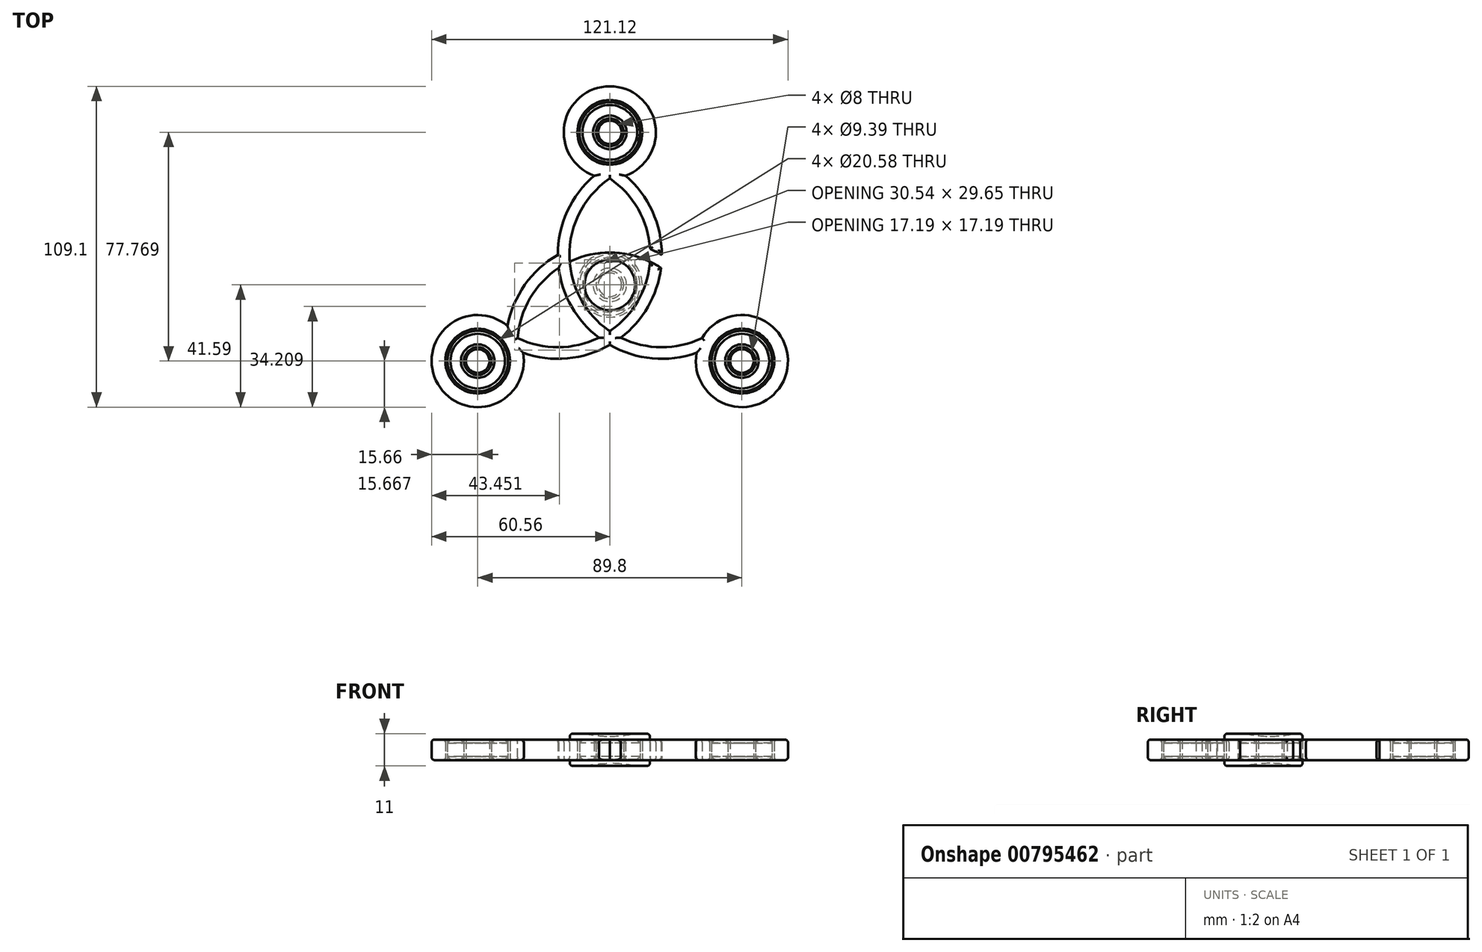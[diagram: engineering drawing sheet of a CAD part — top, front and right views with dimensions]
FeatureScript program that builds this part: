
annotation { "Feature Type Name" : "Feature", "Feature Type Description" : "" }
export const myFeature = defineFeature(function(context is Context, id is Id, definition is map)
    precondition{}
    {
        {
            var Q0;
            Q0=qCreatedBy(makeId("Front.planeOp"),FACE);
            var sketch = newSketch(context, id + "F0", { "sketchPlane" : qUnion([Q0])});
            skLineSegment(sketch, "E0", {"start": v(0, 0) * mm, "end": v(0, 16.34) * mm, "construction": true});
            skSolve(sketch);
        }
        {
            var Q0;
            Q0=qCreatedBy(makeId("Top.planeOp"),FACE);
            var sketch = newSketch(context, id + "F1", { "sketchPlane" : qUnion([Q0])});
            skCircle(sketch, "E1.cCircle", {"center": v(0, 0) * mm, "radius": 40.85 * mm, "construction": true});
            skLineSegment(sketch, "E1.0", {"start": v(0, 40.85) * mm, "end": v(35.37, -20.42) * mm, "construction": true});
            skLineSegment(sketch, "E1.1", {"start": v(35.37, -20.42) * mm, "end": v(-35.37, -20.42) * mm, "construction": true});
            skLineSegment(sketch, "E1.2", {"start": v(-35.37, -20.42) * mm, "end": v(0, 40.85) * mm, "construction": true});
            skCircle(sketch, "E2", {"center": v(0, 40.85) * mm, "radius": 11 * mm, "construction": true});
            skCircle(sketch, "E3", {"center": v(35.37, -20.42) * mm, "radius": 11 * mm, "construction": true});
            skCircle(sketch, "E4", {"center": v(-35.37, -20.42) * mm, "radius": 11 * mm, "construction": true});
            skCircle(sketch, "E5", {"center": v(0, 0) * mm, "radius": 11 * mm, "construction": true});
            skArc(sketch, "E6", {"start": v(10.27, 44.8) * mm, "mid": v(-15.33, -2.5) * mm, "end": v(35.37, -20.42) * mm});
            skArc(sketch, "E7", {"start": v(-35.37, -20.42) * mm, "mid": v(15.33, -2.5) * mm, "end": v(-10.27, 44.8) * mm});
            skArc(sketch, "E8", {"start": v(35.37, -20.42) * mm, "mid": v(0, 14.95) * mm, "end": v(-35.37, -20.42) * mm});
            skLineSegment(sketch, "E9", {"start": v(-35.37, -20.42) * mm, "end": v(-12.95, -7.48) * mm, "construction": true});
            skLineSegment(sketch, "E10.trimOffspring", {"start": v(-9.53, -5.5) * mm, "end": v(0, 0) * mm, "construction": true});
            skLineSegment(sketch, "E11", {"start": v(-12.95, -7.48) * mm, "end": v(-9.53, -5.5) * mm, "construction": true});
            skArc(sketch, "E12.0", {"start": v(11.1, 40.94) * mm, "mid": v(-11.27, -2) * mm, "end": v(35.1, -15.95) * mm});
            skArc(sketch, "E13.0", {"start": v(30.75, -26.88) * mm, "mid": v(-1.6, 10.96) * mm, "end": v(-29.93, -29.98) * mm});
            skArc(sketch, "E14.0", {"start": v(-41, -10.86) * mm, "mid": v(-40.97, -10.9) * mm, "end": v(-40.93, -10.93) * mm});
            skArc(sketch, "E15.trimOffspring", {"start": v(40.93, -10.93) * mm, "mid": v(40.97, -10.9) * mm, "end": v(41, -10.86) * mm});
            skArc(sketch, "E16.trimOffspring", {"start": v(-35.1, -15.95) * mm, "mid": v(11.27, -2) * mm, "end": v(-11.1, 40.94) * mm});
            skLineSegment(sketch, "E17", {"start": v(0, 40.85) * mm, "end": v(0, 36.18) * mm, "construction": true});
            skSolve(sketch);
        }
        {
            var Q0;
            {var subQ0=sQuery(id+"F1.wireOp",EDGE,"E13.0");var subQ1=sQuery(id+"F1.wireOp",EDGE,"E6");var subQ2=makeQuery(id+"F1.imprint","INTERSECT",VERTEX,{"disambiguationData":[OD(0.0)],"derivedFrom":[subQ1,subQ0]});Q0=makeQuery(id+"F1.imprint","IMPRINT",FACE,{"disambiguationData":[TD([[makeQuery(id+"F1.imprint","IMPRINT",EDGE,{"disambiguationData":[TD([[subQ2,1.0]])],"derivedFrom":subQ1}),1.0]])]});}
            var Q1;
            {var subQ0=sQuery(id+"F1.wireOp",EDGE,"E7");var subQ1=sQuery(id+"F1.wireOp",EDGE,"E6");var subQ2=makeQuery(id+"F1.imprint","INTERSECT",VERTEX,{"disambiguationData":[OD(1.0)],"derivedFrom":[subQ1,subQ0]});Q1=makeQuery(id+"F1.imprint","IMPRINT",FACE,{"disambiguationData":[TD([[makeQuery(id+"F1.imprint","IMPRINT",EDGE,{"disambiguationData":[TD([[subQ2,1.0]])],"derivedFrom":subQ1}),1.0]])]});}
            var Q2;
            {var subQ0=sQuery(id+"F1.wireOp",EDGE,"E7");var subQ1=sQuery(id+"F1.wireOp",EDGE,"E6");var subQ2=makeQuery(id+"F1.imprint","INTERSECT",VERTEX,{"disambiguationData":[OD(1.0)],"derivedFrom":[subQ1,subQ0]});Q2=makeQuery(id+"F1.imprint","IMPRINT",FACE,{"disambiguationData":[TD([[makeQuery(id+"F1.imprint","IMPRINT",EDGE,{"disambiguationData":[TD([[subQ2,1.0]])],"derivedFrom":subQ1}),-1.0]])]});}
            var Q3;
            {var subQ0=sQuery(id+"F1.wireOp",EDGE,"E8");var subQ1=sQuery(id+"F1.wireOp",EDGE,"E7");var subQ2=makeQuery(id+"F1.imprint","INTERSECT",VERTEX,{"disambiguationData":[OD(0.0)],"derivedFrom":[subQ1,subQ0]});Q3=makeQuery(id+"F1.imprint","IMPRINT",FACE,{"disambiguationData":[TD([[makeQuery(id+"F1.imprint","IMPRINT",EDGE,{"disambiguationData":[TD([[subQ2,-1.0]])],"derivedFrom":subQ1}),1.0]])]});}
            var Q4;
            {var subQ0=sQuery(id+"F1.wireOp",EDGE,"E8");var subQ1=sQuery(id+"F1.wireOp",EDGE,"E6");var subQ2=makeQuery(id+"F1.imprint","INTERSECT",VERTEX,{"disambiguationData":[OD(1.0)],"derivedFrom":[subQ1,subQ0]});Q4=makeQuery(id+"F1.imprint","IMPRINT",FACE,{"disambiguationData":[TD([[makeQuery(id+"F1.imprint","IMPRINT",EDGE,{"disambiguationData":[TD([[subQ2,-1.0]])],"derivedFrom":subQ1}),-1.0]])]});}
            var Q5;
            {var subQ0=sQuery(id+"F1.wireOp",EDGE,"E13.0");var subQ1=sQuery(id+"F1.wireOp",EDGE,"E6");var subQ2=makeQuery(id+"F1.imprint","INTERSECT",VERTEX,{"disambiguationData":[OD(1.0)],"derivedFrom":[subQ1,subQ0]});Q5=makeQuery(id+"F1.imprint","IMPRINT",FACE,{"disambiguationData":[TD([[makeQuery(id+"F1.imprint","IMPRINT",EDGE,{"disambiguationData":[TD([[subQ2,-1.0]])],"derivedFrom":subQ1}),1.0]])]});}
            var Q6;
            {var subQ0=sQuery(id+"F1.wireOp",EDGE,"E8");var subQ1=sQuery(id+"F1.wireOp",EDGE,"E6");var subQ2=makeQuery(id+"F1.imprint","INTERSECT",VERTEX,{"disambiguationData":[OD(1.0)],"derivedFrom":[subQ1,subQ0]});Q6=makeQuery(id+"F1.imprint","IMPRINT",FACE,{"disambiguationData":[TD([[makeQuery(id+"F1.imprint","IMPRINT",EDGE,{"disambiguationData":[TD([[subQ2,-1.0]])],"derivedFrom":subQ1}),1.0]])]});}
            var Q7;
            {var subQ0=sQuery(id+"F1.wireOp",EDGE,"E12.0");var subQ1=sQuery(id+"F1.wireOp",EDGE,"E7");var subQ2=makeQuery(id+"F1.imprint","INTERSECT",VERTEX,{"disambiguationData":[OD(1.0)],"derivedFrom":[subQ1,subQ0]});Q7=makeQuery(id+"F1.imprint","IMPRINT",FACE,{"disambiguationData":[TD([[makeQuery(id+"F1.imprint","IMPRINT",EDGE,{"disambiguationData":[TD([[subQ2,-1.0]])],"derivedFrom":subQ1}),1.0]])]});}
            var Q8;
            {var subQ0=sQuery(id+"F1.wireOp",EDGE,"E8");var subQ1=sQuery(id+"F1.wireOp",EDGE,"E6");var subQ2=makeQuery(id+"F1.imprint","INTERSECT",VERTEX,{"disambiguationData":[OD(0.0)],"derivedFrom":[subQ1,subQ0]});Q8=makeQuery(id+"F1.imprint","IMPRINT",FACE,{"disambiguationData":[TD([[makeQuery(id+"F1.imprint","IMPRINT",EDGE,{"disambiguationData":[TD([[subQ2,1.0]])],"derivedFrom":subQ1}),1.0]])]});}
            var Q9;
            {var subQ0=sQuery(id+"F1.wireOp",EDGE,"E8");var subQ1=sQuery(id+"F1.wireOp",EDGE,"E7");var subQ2=makeQuery(id+"F1.imprint","INTERSECT",VERTEX,{"disambiguationData":[OD(1.0)],"derivedFrom":[subQ1,subQ0]});Q9=makeQuery(id+"F1.imprint","IMPRINT",FACE,{"disambiguationData":[TD([[makeQuery(id+"F1.imprint","IMPRINT",EDGE,{"disambiguationData":[TD([[subQ2,1.0]])],"derivedFrom":subQ1}),-1.0]])]});}
            var Q10;
            {var subQ0=sQuery(id+"F1.wireOp",EDGE,"E8");var subQ1=sQuery(id+"F1.wireOp",EDGE,"E7");var subQ2=makeQuery(id+"F1.imprint","INTERSECT",VERTEX,{"disambiguationData":[OD(1.0)],"derivedFrom":[subQ1,subQ0]});Q10=makeQuery(id+"F1.imprint","IMPRINT",FACE,{"disambiguationData":[TD([[makeQuery(id+"F1.imprint","IMPRINT",EDGE,{"disambiguationData":[TD([[subQ2,1.0]])],"derivedFrom":subQ1}),1.0]])]});}
            var Q11;
            {var subQ0=sQuery(id+"F1.wireOp",EDGE,"E16.trimOffspring");var subQ1=sQuery(id+"F1.wireOp",EDGE,"E8");var subQ2=makeQuery(id+"F1.imprint","INTERSECT",VERTEX,{"disambiguationData":[OD(1.0)],"derivedFrom":[subQ1,subQ0]});Q11=makeQuery(id+"F1.imprint","IMPRINT",FACE,{"disambiguationData":[TD([[makeQuery(id+"F1.imprint","IMPRINT",EDGE,{"disambiguationData":[TD([[subQ2,-1.0]])],"derivedFrom":subQ1}),1.0]])]});}
            var Q12;
            {var subQ0=sQuery(id+"F1.wireOp",EDGE,"E16.trimOffspring");var subQ1=sQuery(id+"F1.wireOp",EDGE,"E6");var subQ2=makeQuery(id+"F1.imprint","INTERSECT",VERTEX,{"disambiguationData":[OD(0.0)],"derivedFrom":[subQ1,subQ0]});Q12=makeQuery(id+"F1.imprint","IMPRINT",FACE,{"disambiguationData":[TD([[makeQuery(id+"F1.imprint","IMPRINT",EDGE,{"disambiguationData":[TD([[subQ2,-1.0]])],"derivedFrom":subQ1}),1.0]])]});}
            var Q13;
            {var subQ0=sQuery(id+"F1.wireOp",EDGE,"E7");var subQ1=sQuery(id+"F1.wireOp",EDGE,"E6");var subQ2=makeQuery(id+"F1.imprint","INTERSECT",VERTEX,{"disambiguationData":[OD(0.0)],"derivedFrom":[subQ1,subQ0]});Q13=makeQuery(id+"F1.imprint","IMPRINT",FACE,{"disambiguationData":[TD([[makeQuery(id+"F1.imprint","IMPRINT",EDGE,{"disambiguationData":[TD([[subQ2,-1.0]])],"derivedFrom":subQ1}),1.0]])]});}
            var Q14;
            {var subQ0=sQuery(id+"F1.wireOp",EDGE,"E12.0");var subQ1=sQuery(id+"F1.wireOp",EDGE,"E7");var subQ2=makeQuery(id+"F1.imprint","INTERSECT",VERTEX,{"disambiguationData":[OD(0.0)],"derivedFrom":[subQ1,subQ0]});Q14=makeQuery(id+"F1.imprint","IMPRINT",FACE,{"disambiguationData":[TD([[makeQuery(id+"F1.imprint","IMPRINT",EDGE,{"disambiguationData":[TD([[subQ2,1.0]])],"derivedFrom":subQ1}),1.0]])]});}
            extrude(context, id + "F2", {"entities" : qUnion([Q0, Q1, Q2, Q3, Q4, Q5, Q6, Q7, Q8, Q9, Q10, Q11, Q12, Q13, Q14]), "endBound" : BoundingType.SYMMETRIC, "depth" : 7 * mm, "offsetDistance" : 25 * mm});
        }
        {
            var Q0;
            Q0=qCreatedBy(makeId("Top.planeOp"),FACE);
            var sketch = newSketch(context, id + "F3", { "sketchPlane" : qUnion([Q0])});
            skLineSegment(sketch, "E18", {"start": v(0, 0) * mm, "end": v(0, 40.85) * mm, "construction": true});
            skLineSegment(sketch, "E19", {"start": v(0, 40.85) * mm, "end": v(0, 51.85) * mm, "construction": true});
            skCircle(sketch, "E20", {"center": v(0, 51.85) * mm, "radius": 11 * mm});
            skCircle(sketch, "E21.0", {"center": v(0, 51.85) * mm, "radius": 15.66 * mm});
            skCircle(sketch, "E22.1.0", {"center": v(-44.9, -25.92) * mm, "radius": 11 * mm});
            skCircle(sketch, "E22.1.1", {"center": v(-44.9, -25.92) * mm, "radius": 15.66 * mm});
            skCircle(sketch, "E22.2.0", {"center": v(44.9, -25.92) * mm, "radius": 11 * mm});
            skCircle(sketch, "E22.2.1", {"center": v(44.9, -25.92) * mm, "radius": 15.66 * mm});
            skPoint(sketch, "E22.center", {"position": v(0, 0) * mm});
            skSolve(sketch);
        }
        {
            var Q0;
            Q0 = qSketchRegion(id + "F3", true);
            extrude(context, id + "F4", {"entities" : qUnion([Q0]), "operationType" : NewBodyOperationType.ADD, "endBound" : BoundingType.SYMMETRIC, "depth" : 7 * mm, "offsetDistance" : 25 * mm});
        }
        {
            var Q0;
            Q0=makeQuery(id+"F4.boolean.opBoolean","MERGE",FACE,{"derivedFrom":[makeQuery(id+"F2.opExtrude","CAP_FACE",FACE,{"disambiguationData":[OSD([sQuery(id+"F1.wireOp",EDGE,"E6"),sQuery(id+"F1.wireOp",EDGE,"E7"),sQuery(id+"F1.wireOp",EDGE,"E8"),sQuery(id+"F1.wireOp",EDGE,"E12.0"),sQuery(id+"F1.wireOp",EDGE,"E13.0"),sQuery(id+"F1.wireOp",EDGE,"E16.trimOffspring")])],"isStart":true}),makeQuery(id+"F4.opExtrude","CAP_FACE",FACE,{"disambiguationData":[OSD([sQuery(id+"F3.wireOp",EDGE,"E20"),sQuery(id+"F3.wireOp",EDGE,"E21.0")])],"isStart":true}),makeQuery(id+"F4.opExtrude","CAP_FACE",FACE,{"disambiguationData":[OSD([sQuery(id+"F3.wireOp",EDGE,"E22.1.0"),sQuery(id+"F3.wireOp",EDGE,"E22.1.1")])],"isStart":true}),makeQuery(id+"F4.opExtrude","CAP_FACE",FACE,{"disambiguationData":[OSD([sQuery(id+"F3.wireOp",EDGE,"E22.2.0"),sQuery(id+"F3.wireOp",EDGE,"E22.2.1")])],"isStart":true})]});
            var Q1;
            Q1=makeQuery(id+"F4.boolean.opBoolean","MERGE",FACE,{"derivedFrom":[makeQuery(id+"F2.opExtrude","CAP_FACE",FACE,{"disambiguationData":[OSD([sQuery(id+"F1.wireOp",EDGE,"E6"),sQuery(id+"F1.wireOp",EDGE,"E7"),sQuery(id+"F1.wireOp",EDGE,"E8"),sQuery(id+"F1.wireOp",EDGE,"E12.0"),sQuery(id+"F1.wireOp",EDGE,"E13.0"),sQuery(id+"F1.wireOp",EDGE,"E16.trimOffspring")])],"isStart":false}),makeQuery(id+"F4.opExtrude","CAP_FACE",FACE,{"disambiguationData":[OSD([sQuery(id+"F3.wireOp",EDGE,"E20"),sQuery(id+"F3.wireOp",EDGE,"E21.0")])],"isStart":false}),makeQuery(id+"F4.opExtrude","CAP_FACE",FACE,{"disambiguationData":[OSD([sQuery(id+"F3.wireOp",EDGE,"E22.1.0"),sQuery(id+"F3.wireOp",EDGE,"E22.1.1")])],"isStart":false}),makeQuery(id+"F4.opExtrude","CAP_FACE",FACE,{"disambiguationData":[OSD([sQuery(id+"F3.wireOp",EDGE,"E22.2.0"),sQuery(id+"F3.wireOp",EDGE,"E22.2.1")])],"isStart":false})]});
            fillet(context, id + "F5", {"entities" : qUnion([Q0, Q1]), "radius" : 1 * mm, "tangentPropagation" : true, "allowEdgeOverflow" : false});
        }
        {
            var Q0;
            Q0=qCreatedBy(makeId("Top.planeOp"),FACE);
            var sketch = newSketch(context, id + "F6", { "sketchPlane" : qUnion([Q0])});
            skCircle(sketch, "E23", {"center": v(0, 0) * mm, "radius": 11 * mm});
            skCircle(sketch, "E24", {"center": v(0, 0) * mm, "radius": 4 * mm});
            skCircle(sketch, "E25", {"center": v(0, 0) * mm, "radius": 4.7 * mm});
            skCircle(sketch, "E26", {"center": v(0, 0) * mm, "radius": 10.3 * mm});
            skSolve(sketch);
        }
        {
            var Q0;
            Q0=makeQuery(id+"F6.imprint","IMPRINT",FACE,{"disambiguationData":[TD([[makeQuery(id+"F6.imprint","IMPRINT",EDGE,{"derivedFrom":sQuery(id+"F6.wireOp",EDGE,"E24")}),-1.0]])]});
            var Q1;
            Q1=makeQuery(id+"F6.imprint","IMPRINT",FACE,{"disambiguationData":[TD([[makeQuery(id+"F6.imprint","IMPRINT",EDGE,{"derivedFrom":sQuery(id+"F6.wireOp",EDGE,"E23")}),1.0]])]});
            extrude(context, id + "F7", {"entities" : qUnion([Q0, Q1]), "operationType" : NewBodyOperationType.ADD, "endBound" : BoundingType.SYMMETRIC, "depth" : 7 * mm, "offsetDistance" : 25 * mm});
        }
        {
            var Q0;
            Q0=makeQuery(id+"F6.imprint","IMPRINT",FACE,{"disambiguationData":[TD([[makeQuery(id+"F6.imprint","IMPRINT",EDGE,{"derivedFrom":sQuery(id+"F6.wireOp",EDGE,"E25")}),-1.0]])]});
            extrude(context, id + "F8", {"entities" : qUnion([Q0]), "endBound" : BoundingType.SYMMETRIC, "depth" : 6.5 * mm, "offsetDistance" : 25 * mm});
        }
        {
            var Q0;
            Q0=makeQuery(id+"F8.opExtrude","CAP_EDGE",EDGE,{"disambiguationData":[OSD([sQuery(id+"F6.wireOp",EDGE,"E26")])],"isStart":false});
            var Q1;
            Q1=makeQuery(id+"F8.opExtrude","CAP_EDGE",EDGE,{"disambiguationData":[OSD([sQuery(id+"F6.wireOp",EDGE,"E25")])],"isStart":false});
            chamfer(context, id + "F9", {"entities" : qUnion([Q0, Q1]), "chamferType" : ChamferType.OFFSET_ANGLE, "width" : 1 * mm, "oppositeDirection" : false, "angle" : 45 * degree, "tangentPropagation" : true});
        }
        {
            var Q0;
            Q0=makeQuery(id+"F8.opExtrude","CAP_EDGE",EDGE,{"disambiguationData":[OSD([sQuery(id+"F6.wireOp",EDGE,"E25")])],"isStart":true});
            var Q1;
            Q1=makeQuery(id+"F8.opExtrude","CAP_EDGE",EDGE,{"disambiguationData":[OSD([sQuery(id+"F6.wireOp",EDGE,"E26")])],"isStart":true});
            chamfer(context, id + "F10", {"entities" : qUnion([Q0, Q1]), "width" : 1 * mm, "tangentPropagation" : true});
        }
        {
            var Q0;
            Q0=makeQuery(id+"F7.opExtrude","CAP_EDGE",EDGE,{"disambiguationData":[OSD([sQuery(id+"F6.wireOp",EDGE,"E23")])],"isStart":false});
            var Q1;
            Q1=makeQuery(id+"F7.opExtrude","CAP_EDGE",EDGE,{"disambiguationData":[OSD([sQuery(id+"F6.wireOp",EDGE,"E26")])],"isStart":false});
            fillet(context, id + "F11", {"entities" : qUnion([Q0, Q1]), "radius" : .2 * mm, "tangentPropagation" : true, "allowEdgeOverflow" : false});
        }
        {
            var Q0;
            Q0=makeQuery(id+"F7.opExtrude","CAP_EDGE",EDGE,{"disambiguationData":[OSD([sQuery(id+"F6.wireOp",EDGE,"E24")])],"isStart":false});
            var Q1;
            Q1=makeQuery(id+"F7.opExtrude","CAP_EDGE",EDGE,{"disambiguationData":[OSD([sQuery(id+"F6.wireOp",EDGE,"E25")])],"isStart":false});
            var Q2;
            Q2=makeQuery(id+"F7.opExtrude","CAP_EDGE",EDGE,{"disambiguationData":[OSD([sQuery(id+"F6.wireOp",EDGE,"E23")])],"isStart":true});
            var Q3;
            Q3=makeQuery(id+"F7.opExtrude","CAP_EDGE",EDGE,{"disambiguationData":[OSD([sQuery(id+"F6.wireOp",EDGE,"E26")])],"isStart":true});
            var Q4;
            Q4=makeQuery(id+"F7.opExtrude","CAP_EDGE",EDGE,{"disambiguationData":[OSD([sQuery(id+"F6.wireOp",EDGE,"E25")])],"isStart":true});
            var Q5;
            Q5=makeQuery(id+"F7.opExtrude","CAP_EDGE",EDGE,{"disambiguationData":[OSD([sQuery(id+"F6.wireOp",EDGE,"E24")])],"isStart":true});
            fillet(context, id + "F12", {"entities" : qUnion([Q0, Q1, Q2, Q3, Q4, Q5]), "radius" : .2 * mm, "tangentPropagation" : true, "allowEdgeOverflow" : false});
        }
        {
            var Q0;
            Q0=qCreatedBy(makeId("Top.planeOp"),FACE);
            var sketch = newSketch(context, id + "F13", { "sketchPlane" : qUnion([Q0])});
            skLineSegment(sketch, "E27", {"start": v(0, 0) * mm, "end": v(0, 32) * mm, "construction": true});
            skSolve(sketch);
        }
        {
            var Q0;
            Q0=makeQuery(id+"F7.opExtrude","SWEPT_BODY",BODY,{"disambiguationData":[OSD([sQuery(id+"F6.wireOp",EDGE,"E23"),sQuery(id+"F6.wireOp",EDGE,"E26")])]});
            var Q1;
            Q1=makeQuery(id+"F7.opExtrude","SWEPT_BODY",BODY,{"disambiguationData":[OSD([sQuery(id+"F6.wireOp",EDGE,"E24"),sQuery(id+"F6.wireOp",EDGE,"E25")])]});
            var Q2;
            Q2=makeQuery(id+"F8.opExtrude","SWEPT_BODY",BODY,{"disambiguationData":[OSD([sQuery(id+"F6.wireOp",EDGE,"E25"),sQuery(id+"F6.wireOp",EDGE,"E26")])]});
            var Q3;
            Q3=sQuery(id+"F13.wireOp",EDGE,"E27");
            var Q4;
            Q4=sQuery(id+"F13.wireOp",EDGE,"E27");
            transform(context, id + "F14", {"entities" : qUnion([Q0, Q1, Q2]), "transformType" : TransformType.TRANSLATION_DISTANCE, "transformDirection" : qUnion([Q4]), "distance" : 51.85 * mm, "makeCopy" : true});
        }
        {
            var Q0;
            Q0=makeQuery(id+"F14.opPattern","COPY",BODY,{"derivedFrom":makeQuery(id+"F8.opExtrude","SWEPT_BODY",BODY,{"disambiguationData":[OSD([sQuery(id+"F6.wireOp",EDGE,"E25"),sQuery(id+"F6.wireOp",EDGE,"E26")])]}),"instanceName":"1"});
            var Q1;
            Q1=makeQuery(id+"F14.opPattern","COPY",BODY,{"derivedFrom":makeQuery(id+"F7.opExtrude","SWEPT_BODY",BODY,{"disambiguationData":[OSD([sQuery(id+"F6.wireOp",EDGE,"E24"),sQuery(id+"F6.wireOp",EDGE,"E25")])]}),"instanceName":"1"});
            var Q2;
            Q2=makeQuery(id+"F14.opPattern","COPY",BODY,{"derivedFrom":makeQuery(id+"F7.opExtrude","SWEPT_BODY",BODY,{"disambiguationData":[OSD([sQuery(id+"F6.wireOp",EDGE,"E23"),sQuery(id+"F6.wireOp",EDGE,"E26")])]}),"instanceName":"1"});
            var Q3;
            Q3=sQuery(id+"F0.wireOp",EDGE,"E0");
            circularPattern(context, id + "F15", {"entities" : qUnion([Q0, Q1, Q2]), "axis" : qUnion([Q3]), "angle" : 360 * degree, "instanceCount" : 3, "equalSpace" : true});
        }
        {
            var Q0;
            Q0=makeQuery(id+"F7.opExtrude","CAP_FACE",FACE,{"disambiguationData":[OSD([sQuery(id+"F6.wireOp",EDGE,"E24"),sQuery(id+"F6.wireOp",EDGE,"E25")])],"isStart":false});
            var sketch = newSketch(context, id + "F16", { "sketchPlane" : qUnion([Q0])});
            skArc(sketch, "E28.0", {"start": v(13.65, 7.88) * mm, "mid": v(0, 11) * mm, "end": v(-13.65, 7.88) * mm});
            skArc(sketch, "E29.trimOffspring", {"start": v(0, -15.76) * mm, "mid": v(9.53, -5.5) * mm, "end": v(13.65, 7.88) * mm});
            skArc(sketch, "E30.trimOffspring", {"start": v(-13.65, 7.88) * mm, "mid": v(-9.53, -5.5) * mm, "end": v(0, -15.76) * mm});
            skSolve(sketch);
        }
        {
            var Q0;
            Q0 = qSketchRegion(id + "F16", true);
            extrude(context, id + "F17", {"entities" : qUnion([Q0]), "depth" : 2 * mm, "offsetDistance" : 25 * mm});
        }
        {
            var Q0;
            Q0=qCreatedBy(makeId("Front.planeOp"),FACE);
            var sketch = newSketch(context, id + "F18", { "sketchPlane" : qUnion([Q0])});
            skArc(sketch, "E31", {"start": v(0, 4.6) * mm, "mid": v(41.52, 46.12) * mm, "end": v(0, 87.64) * mm});
            skLineSegment(sketch, "E32", {"start": v(0, 46.12) * mm, "end": v(0, 4.6) * mm});
            skLineSegment(sketch, "E33", {"start": v(0, 46.12) * mm, "end": v(0, 87.64) * mm});
            skSolve(sketch);
        }
        {
            var Q0;
            Q0=makeQuery(id+"F18.imprint","IMPRINT",FACE,{"disambiguationData":[TD([[makeQuery(id+"F18.imprint","IMPRINT",EDGE,{"derivedFrom":sQuery(id+"F18.wireOp",EDGE,"E31")}),1.0]])]});
            var Q1;
            Q1=sQuery(id+"F18.wireOp",EDGE,"E33");
            revolve(context, id + "F19", {"surfaceOperationType" : NewSurfaceOperationType.NEW, "entities" : qUnion([Q0]), "axis" : qUnion([Q1]), "revolveType" : RevolveType.FULL});
        }
        {
            var Q0;
            Q0=makeQuery(id+"F19.opRevolve","SWEPT_BODY",BODY,{"disambiguationData":[OSD([sQuery(id+"F18.wireOp",EDGE,"E31"),sQuery(id+"F18.wireOp",EDGE,"E32"),sQuery(id+"F18.wireOp",EDGE,"E33")])]});
            var Q1;
            Q1=makeQuery(id+"F17.opExtrude","SWEPT_BODY",BODY,{"disambiguationData":[OSD([sQuery(id+"F16.wireOp",EDGE,"E28.0"),sQuery(id+"F16.wireOp",EDGE,"E29.trimOffspring"),sQuery(id+"F16.wireOp",EDGE,"E30.trimOffspring")])]});
            booleanBodies(context, id + "F20", {"operationType" : BooleanOperationType.SUBTRACTION, "tools" : qUnion([Q0]), "targets" : qUnion([Q1])});
        }
        {
            var Q0;
            Q0=makeQuery(id+"F17.opExtrude","CAP_EDGE",EDGE,{"disambiguationData":[OSD([sQuery(id+"F16.wireOp",EDGE,"E29.trimOffspring")])],"isStart":false});
            var Q1;
            {var subQ0=sQuery(id+"F1.wireOp",EDGE,"E16.trimOffspring");var subQ1=sQuery(id+"F1.wireOp",EDGE,"E12.0");var subQ2=sQuery(id+"F1.wireOp",EDGE,"E8");Q1=makeQuery(id+"F5.opFillet","BLEND_EDGE",EDGE,{"blendedFrom":[makeQuery(id+"F2.opExtrude","CAP_EDGE",EDGE,{"disambiguationData":[OSD([subQ2]),TDD([makeQuery(id+"F1.imprint","IMPRINT",EDGE,{"disambiguationData":[TD([[makeQuery(id+"F1.imprint","INTERSECT",VERTEX,{"disambiguationData":[OD(1.0)],"derivedFrom":[subQ2,subQ0]}),-1.0]])],"derivedFrom":subQ2})])],"isStart":false}),makeQuery(id+"F4.boolean.opBoolean","MERGE",FACE,{"derivedFrom":[makeQuery(id+"F2.opExtrude","CAP_FACE",FACE,{"disambiguationData":[OSD([sQuery(id+"F1.wireOp",EDGE,"E6"),sQuery(id+"F1.wireOp",EDGE,"E7"),subQ2,subQ1,sQuery(id+"F1.wireOp",EDGE,"E13.0"),subQ0])],"isStart":false}),makeQuery(id+"F4.opExtrude","CAP_FACE",FACE,{"disambiguationData":[OSD([sQuery(id+"F3.wireOp",EDGE,"E20"),sQuery(id+"F3.wireOp",EDGE,"E21.0")])],"isStart":false}),makeQuery(id+"F4.opExtrude","CAP_FACE",FACE,{"disambiguationData":[OSD([sQuery(id+"F3.wireOp",EDGE,"E22.1.0"),sQuery(id+"F3.wireOp",EDGE,"E22.1.1")])],"isStart":false}),makeQuery(id+"F4.opExtrude","CAP_FACE",FACE,{"disambiguationData":[OSD([sQuery(id+"F3.wireOp",EDGE,"E22.2.0"),sQuery(id+"F3.wireOp",EDGE,"E22.2.1")])],"isStart":false})]})],"blendedInto":[makeQuery(id+"F4.boolean.opBoolean","MERGE",FACE,{"derivedFrom":[makeQuery(id+"F2.opExtrude","CAP_FACE",FACE,{"disambiguationData":[OSD([sQuery(id+"F1.wireOp",EDGE,"E6"),sQuery(id+"F1.wireOp",EDGE,"E7"),subQ2,subQ1,sQuery(id+"F1.wireOp",EDGE,"E13.0"),subQ0])],"isStart":false}),makeQuery(id+"F4.opExtrude","CAP_FACE",FACE,{"disambiguationData":[OSD([sQuery(id+"F3.wireOp",EDGE,"E20"),sQuery(id+"F3.wireOp",EDGE,"E21.0")])],"isStart":false}),makeQuery(id+"F4.opExtrude","CAP_FACE",FACE,{"disambiguationData":[OSD([sQuery(id+"F3.wireOp",EDGE,"E22.1.0"),sQuery(id+"F3.wireOp",EDGE,"E22.1.1")])],"isStart":false}),makeQuery(id+"F4.opExtrude","CAP_FACE",FACE,{"disambiguationData":[OSD([sQuery(id+"F3.wireOp",EDGE,"E22.2.0"),sQuery(id+"F3.wireOp",EDGE,"E22.2.1")])],"isStart":false})]})]});}
            var Q2;
            Q2=makeQuery(id+"F17.opExtrude","CAP_EDGE",EDGE,{"disambiguationData":[OSD([sQuery(id+"F16.wireOp",EDGE,"E30.trimOffspring")])],"isStart":false});
            var Q3;
            Q3=makeQuery(id+"F17.opExtrude","SWEPT_EDGE",EDGE,{"disambiguationData":[OSD([sQuery(id+"F16.wireOp",EDGE,"E29.trimOffspring"),sQuery(id+"F16.wireOp",EDGE,"E30.trimOffspring")])]});
            var Q4;
            Q4=makeQuery(id+"F17.opExtrude","SWEPT_EDGE",EDGE,{"disambiguationData":[OSD([sQuery(id+"F16.wireOp",EDGE,"E28.0"),sQuery(id+"F16.wireOp",EDGE,"E29.trimOffspring")])]});
            var Q5;
            Q5=makeQuery(id+"F17.opExtrude","CAP_EDGE",EDGE,{"disambiguationData":[OSD([sQuery(id+"F16.wireOp",EDGE,"E28.0")])],"isStart":false});
            var Q6;
            Q6=makeQuery(id+"F17.opExtrude","SWEPT_EDGE",EDGE,{"disambiguationData":[OSD([sQuery(id+"F16.wireOp",EDGE,"E28.0"),sQuery(id+"F16.wireOp",EDGE,"E30.trimOffspring")])]});
            fillet(context, id + "F21", {"entities" : qUnion([Q0, Q1, Q2, Q3, Q4, Q5, Q6]), "radius" : 1 * mm, "tangentPropagation" : true, "allowEdgeOverflow" : false});
        }
        {
            var Q0;
            Q0=makeQuery(id+"F17.opExtrude","SWEPT_BODY",BODY,{"disambiguationData":[OSD([sQuery(id+"F16.wireOp",EDGE,"E28.0"),sQuery(id+"F16.wireOp",EDGE,"E29.trimOffspring"),sQuery(id+"F16.wireOp",EDGE,"E30.trimOffspring")])]});
            var Q1;
            Q1=qCreatedBy(makeId("Top.planeOp"),FACE);
            mirror(context, id + "F22", {"entities" : qUnion([Q0]), "mirrorPlane" : qUnion([Q1])});
        }
    });
